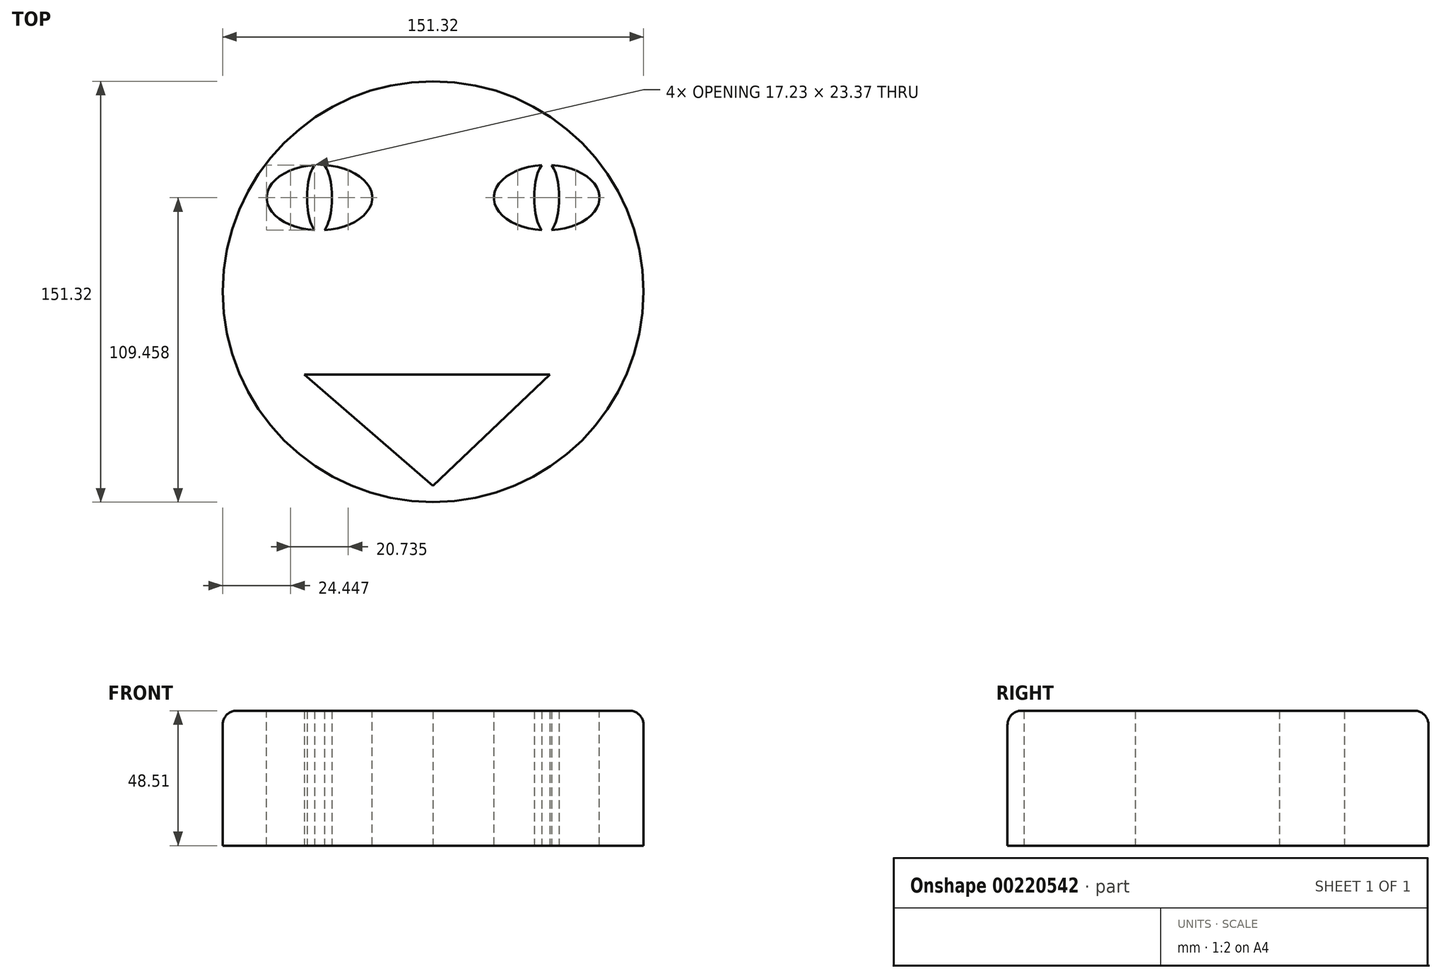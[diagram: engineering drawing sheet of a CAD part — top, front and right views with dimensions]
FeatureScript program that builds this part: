
annotation { "Feature Type Name" : "Feature", "Feature Type Description" : "" }
export const myFeature = defineFeature(function(context is Context, id is Id, definition is map)
    precondition{}
    {
        {
            var Q0;
            Q0=qCreatedBy(makeId("Top.planeOp"),FACE);
            var sketch = newSketch(context, id + "F0", { "sketchPlane" : qUnion([Q0])});
            skCircle(sketch, "E0", {"center": v(0, 0) * mm, "radius": 75.66 * mm});
            skEllipse(sketch, "E1", {"center": v(-40.85, 33.8) * mm, "majorRadius": 18.98 * mm, "minorRadius": 11.73 * mm, "majorAxis": v(1, 0)});
            skEllipse(sketch, "E2.MirrorC", {"center": v(40.85, 33.8) * mm, "majorRadius": 18.98 * mm, "minorRadius": 11.73 * mm, "majorAxis": v(-1, 0)});
            skEllipse(sketch, "E3", {"center": v(-40.85, 33.8) * mm, "majorRadius": 12.7 * mm, "minorRadius": 4.49 * mm, "majorAxis": v(0, -1)});
            skEllipse(sketch, "E4.MirrorC", {"center": v(40.85, 33.8) * mm, "majorRadius": 12.7 * mm, "minorRadius": 4.49 * mm, "majorAxis": v(0, -1)});
            skLineSegment(sketch, "E5", {"start": v(-46.31, -29.77) * mm, "end": v(42, -29.77) * mm});
            skLineSegment(sketch, "E6", {"start": v(42, -29.77) * mm, "end": v(0, -69.75) * mm});
            skLineSegment(sketch, "E7", {"start": v(0, -69.75) * mm, "end": v(-46.31, -29.77) * mm});
            skSolve(sketch);
        }
        {
            var Q0;
            Q0=makeQuery(id+"F0.imprint","IMPRINT",FACE,{"disambiguationData":[TD([[makeQuery(id+"F0.imprint","IMPRINT",EDGE,{"derivedFrom":sQuery(id+"F0.wireOp",EDGE,"E0")}),1.0]])]});
            var Q1;
            Q1=makeQuery(id+"F0.imprint","IMPRINT",FACE,{"disambiguationData":[TD([[makeQuery(id+"F0.imprint","IMPRINT",EDGE,{"derivedFrom":sQuery(id+"F0.wireOp",EDGE,"E4.MirrorC")}),1.0]])]});
            var Q2;
            Q2=makeQuery(id+"F0.imprint","IMPRINT",FACE,{"disambiguationData":[TD([[makeQuery(id+"F0.imprint","IMPRINT",EDGE,{"derivedFrom":sQuery(id+"F0.wireOp",EDGE,"E3")}),1.0]])]});
            var Q3;
            {var subQ0=sQuery(id+"F0.wireOp",EDGE,"E4.MirrorC");var subQ1=sQuery(id+"F0.wireOp",EDGE,"E2.MirrorC");var subQ2=makeQuery(id+"F0.imprint","INTERSECT",VERTEX,{"disambiguationData":[OD(0.0)],"derivedFrom":[subQ1,subQ0]});Q3=makeQuery(id+"F0.imprint","IMPRINT",FACE,{"disambiguationData":[TD([[makeQuery(id+"F0.imprint","IMPRINT",EDGE,{"disambiguationData":[TD([[subQ2,1.0]])],"derivedFrom":subQ1}),-1.0]])]});}
            var Q4;
            {var subQ0=sQuery(id+"F0.wireOp",EDGE,"E4.MirrorC");var subQ1=sQuery(id+"F0.wireOp",EDGE,"E2.MirrorC");var subQ2=makeQuery(id+"F0.imprint","INTERSECT",VERTEX,{"disambiguationData":[OD(2.0)],"derivedFrom":[subQ1,subQ0]});Q4=makeQuery(id+"F0.imprint","IMPRINT",FACE,{"disambiguationData":[TD([[makeQuery(id+"F0.imprint","IMPRINT",EDGE,{"disambiguationData":[TD([[subQ2,-1.0]])],"derivedFrom":subQ1}),-1.0]])]});}
            var Q5;
            {var subQ0=sQuery(id+"F0.wireOp",EDGE,"E3");var subQ1=sQuery(id+"F0.wireOp",EDGE,"E1");var subQ2=makeQuery(id+"F0.imprint","INTERSECT",VERTEX,{"disambiguationData":[OD(0.0)],"derivedFrom":[subQ1,subQ0]});Q5=makeQuery(id+"F0.imprint","IMPRINT",FACE,{"disambiguationData":[TD([[makeQuery(id+"F0.imprint","IMPRINT",EDGE,{"disambiguationData":[TD([[subQ2,1.0]])],"derivedFrom":subQ1}),-1.0]])]});}
            var Q6;
            {var subQ0=sQuery(id+"F0.wireOp",EDGE,"E3");var subQ1=sQuery(id+"F0.wireOp",EDGE,"E1");var subQ2=makeQuery(id+"F0.imprint","INTERSECT",VERTEX,{"disambiguationData":[OD(2.0)],"derivedFrom":[subQ1,subQ0]});Q6=makeQuery(id+"F0.imprint","IMPRINT",FACE,{"disambiguationData":[TD([[makeQuery(id+"F0.imprint","IMPRINT",EDGE,{"disambiguationData":[TD([[subQ2,-1.0]])],"derivedFrom":subQ1}),-1.0]])]});}
            extrude(context, id + "F1", {"entities" : qUnion([Q0, Q1, Q2, Q3, Q4, Q5, Q6]), "depth" : 48.5 * mm});
        }
        {
            var Q0;
            Q0=makeQuery(id+"F1.opExtrude","CAP_EDGE",EDGE,{"disambiguationData":[OSD([sQuery(id+"F0.wireOp",EDGE,"E0")])],"isStart":false});
            fillet(context, id + "F2", {"entities" : qUnion([Q0]), "radius" : 5.08 * mm, "tangentPropagation" : true, "allowEdgeOverflow" : false});
        }
    });
